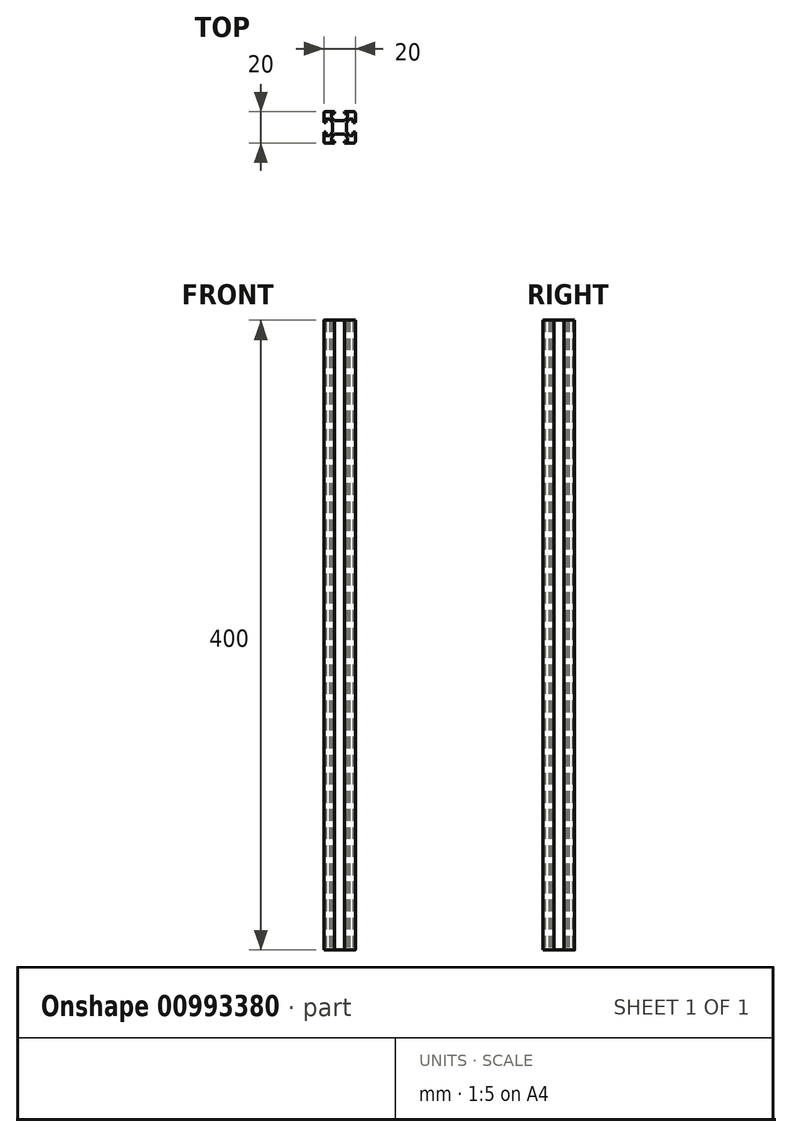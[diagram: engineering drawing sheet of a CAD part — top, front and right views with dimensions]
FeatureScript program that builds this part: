
annotation { "Feature Type Name" : "Feature", "Feature Type Description" : "" }
export const myFeature = defineFeature(function(context is Context, id is Id, definition is map)
    precondition{}
    {
        {
            var Q0;
            Q0=qCreatedBy(makeId("Top.planeOp"),FACE);
            var sketch = newSketch(context, id + "F0", { "sketchPlane" : qUnion([Q0])});
            skLineSegment(sketch, "E0.1", {"start": v(5.65, 6.9) * mm, "end": v(5.65, 13.1) * mm});
            skLineSegment(sketch, "E0.2", {"start": v(6.9, 5.65) * mm, "end": v(13.1, 5.65) * mm});
            skLineSegment(sketch, "E0.3", {"start": v(14.35, 6.9) * mm, "end": v(14.35, 13.1) * mm});
            skLineSegment(sketch, "E1", {"start": v(1, 20) * mm, "end": v(6.9, 20) * mm});
            skLineSegment(sketch, "E2", {"start": v(6.9, 20) * mm, "end": v(6.9, 18.7) * mm});
            skLineSegment(sketch, "E3", {"start": v(6.9, 18.7) * mm, "end": v(4.9, 18.7) * mm});
            skLineSegment(sketch, "E4", {"start": v(6.9, 14.35) * mm, "end": v(4.9, 16.35) * mm});
            skLineSegment(sketch, "E5", {"start": v(4.9, 18.7) * mm, "end": v(4.9, 16.35) * mm});
            skLineSegment(sketch, "E6.MirrorCS", {"start": v(0, 13.1) * mm, "end": v(1.3, 13.1) * mm});
            skLineSegment(sketch, "E7.MirrorCS", {"start": v(1.3, 13.1) * mm, "end": v(1.3, 15.1) * mm});
            skLineSegment(sketch, "E8.MirrorCS", {"start": v(1.3, 15.1) * mm, "end": v(3.65, 15.1) * mm});
            skLineSegment(sketch, "E9.MirrorCS", {"start": v(5.65, 13.1) * mm, "end": v(3.65, 15.1) * mm});
            skLineSegment(sketch, "E10", {"start": v(0, 19) * mm, "end": v(0, 13.1) * mm});
            skLineSegment(sketch, "E11.MirrorCS", {"start": v(13.1, 14.35) * mm, "end": v(15.1, 16.35) * mm});
            skLineSegment(sketch, "E12.MirrorCS", {"start": v(13.1, 18.7) * mm, "end": v(15.1, 18.7) * mm});
            skLineSegment(sketch, "E13.MirrorCS", {"start": v(13.1, 20) * mm, "end": v(13.1, 18.7) * mm});
            skLineSegment(sketch, "E14.MirrorCS", {"start": v(15.1, 18.7) * mm, "end": v(15.1, 16.35) * mm});
            skLineSegment(sketch, "E15.MirrorCS", {"start": v(14.35, 13.1) * mm, "end": v(16.35, 15.1) * mm});
            skLineSegment(sketch, "E16.MirrorCS", {"start": v(18.7, 15.1) * mm, "end": v(16.35, 15.1) * mm});
            skLineSegment(sketch, "E17.MirrorCS", {"start": v(18.7, 13.1) * mm, "end": v(18.7, 15.1) * mm});
            skLineSegment(sketch, "E18.MirrorCS", {"start": v(20, 13.1) * mm, "end": v(18.7, 13.1) * mm});
            skLineSegment(sketch, "E19.MirrorCS", {"start": v(20, 19) * mm, "end": v(20, 13.1) * mm});
            skLineSegment(sketch, "E20.MirrorCS", {"start": v(19, 20) * mm, "end": v(13.1, 20) * mm});
            skLineSegment(sketch, "E21.MirrorCS", {"start": v(0, 6.9) * mm, "end": v(1.3, 6.9) * mm});
            skLineSegment(sketch, "E22.MirrorCS", {"start": v(4.9, 1.3) * mm, "end": v(4.9, 3.65) * mm});
            skLineSegment(sketch, "E23.MirrorCS", {"start": v(1.3, 4.9) * mm, "end": v(3.65, 4.9) * mm});
            skLineSegment(sketch, "E24.MirrorCS", {"start": v(1.3, 6.9) * mm, "end": v(1.3, 4.9) * mm});
            skLineSegment(sketch, "E25.MirrorCS", {"start": v(5.65, 6.9) * mm, "end": v(3.65, 4.9) * mm});
            skLineSegment(sketch, "E26.MirrorCS", {"start": v(6.9, 5.65) * mm, "end": v(4.9, 3.65) * mm});
            skLineSegment(sketch, "E27.MirrorCS", {"start": v(6.9, 0) * mm, "end": v(6.9, 1.3) * mm});
            skLineSegment(sketch, "E28.MirrorCS", {"start": v(6.9, 1.3) * mm, "end": v(4.9, 1.3) * mm});
            skLineSegment(sketch, "E29.MirrorCS", {"start": v(18.7, 4.9) * mm, "end": v(16.35, 4.9) * mm});
            skLineSegment(sketch, "E30.MirrorCS", {"start": v(20, 6.9) * mm, "end": v(18.7, 6.9) * mm});
            skLineSegment(sketch, "E31.MirrorCS", {"start": v(15.1, 1.3) * mm, "end": v(15.1, 3.65) * mm});
            skLineSegment(sketch, "E32.MirrorCS", {"start": v(13.1, 0) * mm, "end": v(13.1, 1.3) * mm});
            skLineSegment(sketch, "E33.MirrorCS", {"start": v(13.1, 1.3) * mm, "end": v(15.1, 1.3) * mm});
            skLineSegment(sketch, "E34.MirrorCS", {"start": v(18.7, 6.9) * mm, "end": v(18.7, 4.9) * mm});
            skLineSegment(sketch, "E35.MirrorCS", {"start": v(19, 0) * mm, "end": v(13.1, 0) * mm});
            skLineSegment(sketch, "E36.MirrorCS", {"start": v(13.1, 5.65) * mm, "end": v(15.1, 3.65) * mm});
            skLineSegment(sketch, "E37.MirrorCS", {"start": v(20, 1) * mm, "end": v(20, 6.9) * mm});
            skLineSegment(sketch, "E38.MirrorCS", {"start": v(14.35, 6.9) * mm, "end": v(16.35, 4.9) * mm});
            skLineSegment(sketch, "E39", {"start": v(6.9, 14.35) * mm, "end": v(13.1, 14.35) * mm});
            skLineSegment(sketch, "E40", {"start": v(0, 6.9) * mm, "end": v(0, 1) * mm});
            skLineSegment(sketch, "E41", {"start": v(1, 0) * mm, "end": v(6.9, 0) * mm});
            skPoint(sketch, "E42.visualSharp", {"position": v(0, 20) * mm});
            skArc(sketch, "E42.filletArc", {"start": v(1, 20) * mm, "mid": v(0.3, 19.7) * mm, "end": v(0, 19) * mm});
            skPoint(sketch, "E43.visualSharp", {"position": v(20, 20) * mm});
            skArc(sketch, "E43.filletArc", {"start": v(20, 19) * mm, "mid": v(19.7, 19.7) * mm, "end": v(19, 20) * mm});
            skPoint(sketch, "E44.visualSharp", {"position": v(20, 0) * mm});
            skArc(sketch, "E44.filletArc", {"start": v(19, 0) * mm, "mid": v(19.7, 0.3) * mm, "end": v(20, 1) * mm});
            skPoint(sketch, "E45.visualSharp", {"position": v(0, 0) * mm});
            skArc(sketch, "E45.filletArc", {"start": v(0, 1) * mm, "mid": v(0.3, 0.3) * mm, "end": v(1, 0) * mm});
            skSolve(sketch);
        }
        {
            var Q0;
            Q0=qSketchRegion(id+"F0",true);
            extrude(context, id + "F1", {"entities" : qUnion([Q0]), "depth" : 400 * mm, "offsetDistance" : 25 * mm});
        }
    });
